# Revit family: Platinum_BC_iPlus 4.5_MR_Unidad_Exterior
name_source: partatom
category: Equipos mecánicos
units: mm (PartAtom-declared; Revit-internal decimal feet)

## family parameters
Compartido = No
Corte con vacíos al cargar = No
Cota de conector redondo = Diámetro de uso
Número OmniClass = 23.75.10.21
Punto de cálculo de habitación = No
Se basa en plano de trabajo = No
Siempre vertical = Sí
Tipo de pieza = Normal
Título OmniClass = Heat Pumps

## types (1)
- PLATINUM BC iPLUS 4,5MR (U.E)
    Altura = 880 mm  [stored 2.88714 ft]
    Anchura = 840 mm
    Blanco = Color RGB 216-216-216
    Caudal de aire (m3/min) = 35
    Código de montaje = 7656794
    Descripción = Platinum BC iPlus 4.5 (UE)
    Diametro gas refrigerante = 12.7 mm  [stored 0.0416667 ft]
    Diametro liquido refrigerante = 6.35 mm  [stored 0.0208333 ft]
    Distancia frontal = 500 mm
    Drenaje = 32 mm  [stored 0.104987 ft]
    Fabricante = BAXI
    Fan = Color RGB 100-100-100
    Gris = Color RGB 175-175-175
    Hz = 50 Hz
    IFCExportAs = IfcPumpType
    IFCExportType = NOTDEFINED
    Modelo = Platinum BC iPlus 4.5 MR
    Negro = Color RGB 060-060-060
    Peso (kg) = 42
    Phase = 1
    Potencia Acustica (dB(A)) = 62.4
    Potencia calorífica (kW) = 4.6
    Potencia frigorifica (kW) = 3.8
    Profundidad = 330 mm  [stored 1.08268 ft]
    Revit Version = 2017
    Rojo = Color RGB 255-000-000
    Tipo Refrigerante = R410A
    URL = https://www.baxi.es
    URL PRODUCT = https://www.baxi.es
    Voltage = 230 V

note: [stored X ft] marks values corroborated as IEEE doubles in the binary element streams (Revit-internal decimal feet)

## geometry (parser evidence)
native form markers: Sweep x2
no freeform markers — native parametric forms only
